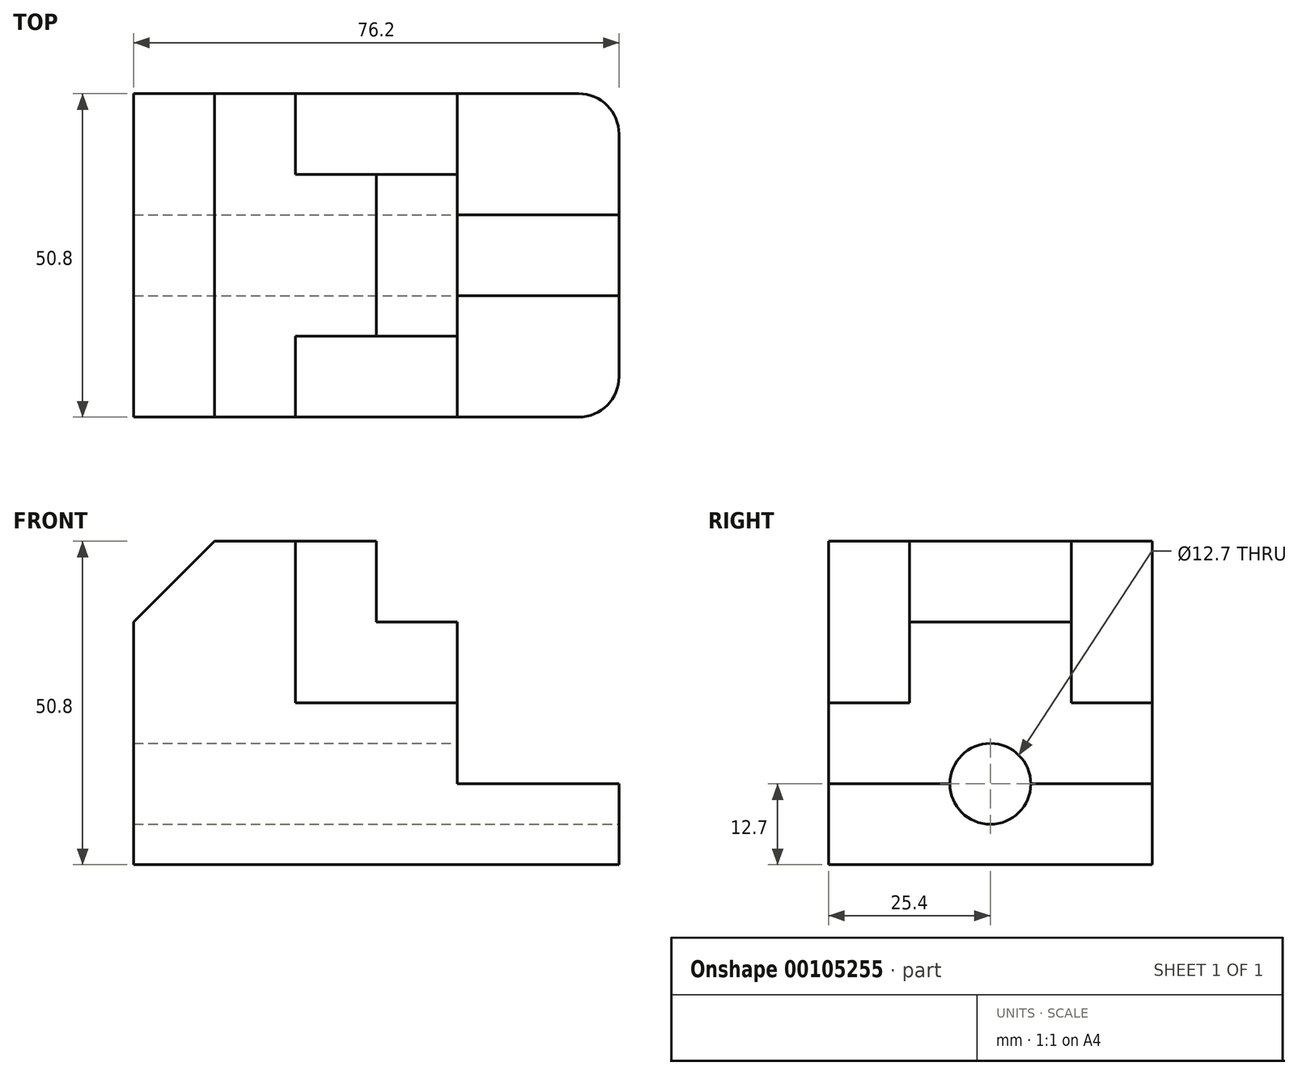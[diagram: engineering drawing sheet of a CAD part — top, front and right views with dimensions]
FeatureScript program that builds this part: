
annotation { "Feature Type Name" : "Feature", "Feature Type Description" : "" }
export const myFeature = defineFeature(function(context is Context, id is Id, definition is map)
    precondition{}
    {
        {
            var Q0;
            Q0=qCreatedBy(makeId("Front.planeOp"),FACE);
            var sketch = newSketch(context, id + "F0", { "sketchPlane" : qUnion([Q0])});
            skLineSegment(sketch, "E0", {"start": v(0, 0) * mm, "end": v(76.2, 0) * mm});
            skLineSegment(sketch, "E1", {"start": v(76.2, 0) * mm, "end": v(76.2, 12.7) * mm});
            skLineSegment(sketch, "E2", {"start": v(76.2, 12.7) * mm, "end": v(50.8, 12.7) * mm});
            skLineSegment(sketch, "E3", {"start": v(50.8, 12.7) * mm, "end": v(50.8, 25.4) * mm});
            skLineSegment(sketch, "E4", {"start": v(50.8, 25.4) * mm, "end": v(25.4, 25.4) * mm});
            skLineSegment(sketch, "E5", {"start": v(25.4, 25.4) * mm, "end": v(25.4, 50.8) * mm});
            skLineSegment(sketch, "E6", {"start": v(25.4, 50.8) * mm, "end": v(12.7, 50.8) * mm});
            skLineSegment(sketch, "E7", {"start": v(12.7, 50.8) * mm, "end": v(0, 38.1) * mm});
            skLineSegment(sketch, "E8", {"start": v(0, 38.1) * mm, "end": v(0, 0) * mm});
            skSolve(sketch);
        }
        {
            var Q0;
            Q0=makeQuery(id+"F0.imprint","IMPRINT",FACE,{"disambiguationData":[TD([[makeQuery(id+"F0.imprint","IMPRINT",EDGE,{"derivedFrom":sQuery(id+"F0.wireOp",EDGE,"E0")}),1.0]])]});
            extrude(context, id + "F1", {"entities" : qUnion([Q0]), "endBound" : BoundingType.SYMMETRIC, "depth" : 50.8 * mm});
        }
        {
            var Q0;
            Q0=qCreatedBy(makeId("Front.planeOp"),FACE);
            var sketch = newSketch(context, id + "F2", { "sketchPlane" : qUnion([Q0])});
            skLineSegment(sketch, "E9", {"start": v(25.4, 25.4) * mm, "end": v(25.4, 50.8) * mm});
            skLineSegment(sketch, "E10", {"start": v(25.4, 50.8) * mm, "end": v(38.1, 50.8) * mm});
            skLineSegment(sketch, "E11", {"start": v(38.1, 50.8) * mm, "end": v(38.1, 38.1) * mm});
            skLineSegment(sketch, "E12", {"start": v(38.1, 38.1) * mm, "end": v(50.8, 38.1) * mm});
            skLineSegment(sketch, "E13", {"start": v(50.8, 38.1) * mm, "end": v(50.8, 25.4) * mm});
            skLineSegment(sketch, "E14", {"start": v(25.4, 25.4) * mm, "end": v(50.8, 25.4) * mm});
            skSolve(sketch);
        }
        {
            var Q0;
            Q0=makeQuery(id+"F2.imprint","IMPRINT",FACE,{"disambiguationData":[TD([[makeQuery(id+"F2.imprint","IMPRINT",EDGE,{"derivedFrom":sQuery(id+"F2.wireOp",EDGE,"E9")}),-1.0]])]});
            extrude(context, id + "F3", {"entities" : qUnion([Q0]), "operationType" : NewBodyOperationType.ADD, "endBound" : BoundingType.SYMMETRIC, "depth" : 25.4 * mm});
        }
        {
            var Q0;
            Q0=makeQuery(id+"F1.opExtrude","SWEPT_FACE",FACE,{"disambiguationData":[OSD([sQuery(id+"F0.wireOp",EDGE,"E1")])]});
            var sketch = newSketch(context, id + "F4", { "sketchPlane" : qUnion([Q0])});
            skCircle(sketch, "E15", {"center": v(0, 12.7) * mm, "radius": 6.35 * mm});
            skSolve(sketch);
        }
        {
            var Q0;
            Q0 = qSketchRegion(id + "F4", true);
            extrude(context, id + "F5", {"entities" : qUnion([Q0]), "operationType" : NewBodyOperationType.REMOVE, "endBound" : BoundingType.THROUGH_ALL, "oppositeDirection" : true, "depth" : 25.4 * mm});
        }
        {
            var Q0;
            Q0=makeQuery(id+"F1.opExtrude","CAP_EDGE",EDGE,{"disambiguationData":[OSD([sQuery(id+"F0.wireOp",EDGE,"E1")])],"isStart":false});
            var Q1;
            Q1=makeQuery(id+"F1.opExtrude","CAP_EDGE",EDGE,{"disambiguationData":[OSD([sQuery(id+"F0.wireOp",EDGE,"E1")])],"isStart":true});
            fillet(context, id + "F6", {"entities" : qUnion([Q0, Q1]), "radius" : 6.35 * mm, "tangentPropagation" : true, "allowEdgeOverflow" : false});
        }
    });
